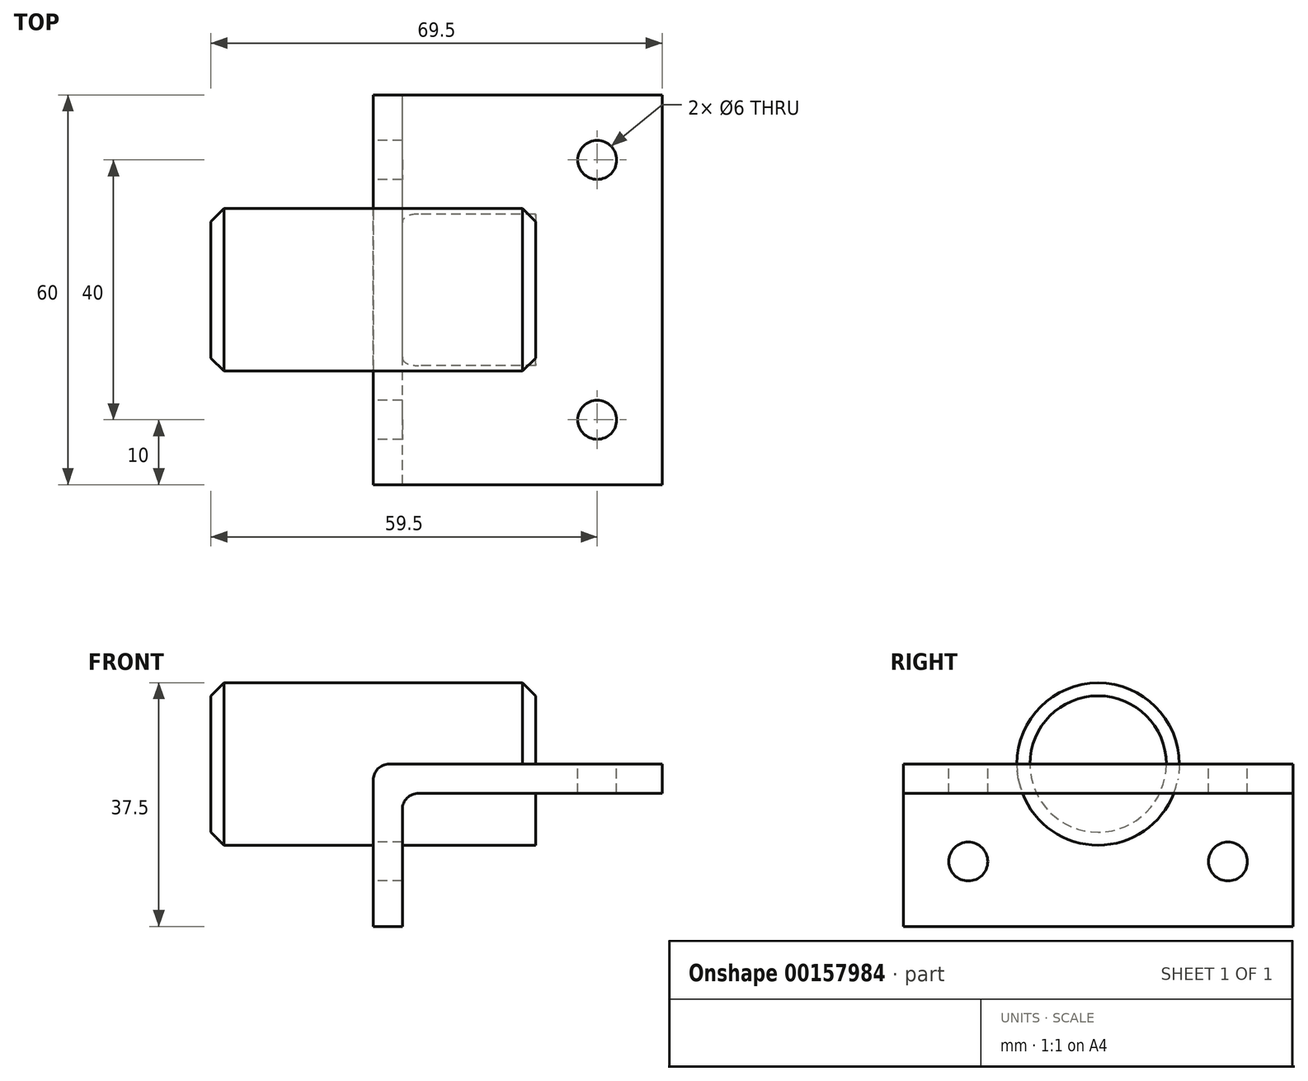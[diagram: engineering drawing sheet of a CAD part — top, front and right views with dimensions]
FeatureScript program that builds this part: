
annotation { "Feature Type Name" : "Feature", "Feature Type Description" : "" }
export const myFeature = defineFeature(function(context is Context, id is Id, definition is map)
    precondition{}
    {
        {
            var Q0;
            Q0=qCreatedBy(makeId("Front.planeOp"),FACE);
            var sketch = newSketch(context, id + "F0", { "sketchPlane" : qUnion([Q0])});
            skLineSegment(sketch, "E0", {"start": v(2.5, 0) * mm, "end": v(44.5, 0) * mm});
            skLineSegment(sketch, "E1", {"start": v(44.5, 0) * mm, "end": v(44.5, -4.5) * mm});
            skLineSegment(sketch, "E2", {"start": v(44.5, -4.5) * mm, "end": v(7, -4.5) * mm});
            skLineSegment(sketch, "E3", {"start": v(4.5, -7) * mm, "end": v(4.5, -25) * mm});
            skLineSegment(sketch, "E4", {"start": v(4.5, -25) * mm, "end": v(0, -25) * mm});
            skLineSegment(sketch, "E5", {"start": v(0, -25) * mm, "end": v(0, -2.5) * mm});
            skPoint(sketch, "E6.visualSharp", {"position": v(4.5, -4.5) * mm});
            skArc(sketch, "E6.filletArc", {"start": v(7, -4.5) * mm, "mid": v(5.23, -5.23) * mm, "end": v(4.5, -7) * mm});
            skPoint(sketch, "E7.visualSharp", {"position": v(0, 0) * mm});
            skArc(sketch, "E7.filletArc", {"start": v(2.5, 0) * mm, "mid": v(0.73, -0.73) * mm, "end": v(0, -2.5) * mm});
            skSolve(sketch);
        }
        {
            var Q0;
            Q0 = qSketchRegion(id + "F0", true);
            extrude(context, id + "F1", {"entities" : qUnion([Q0]), "endBound" : BoundingType.SYMMETRIC, "depth" : 60 * mm});
        }
        {
            var Q0;
            Q0=qCreatedBy(makeId("Right.planeOp"),FACE);
            var sketch = newSketch(context, id + "F2", { "sketchPlane" : qUnion([Q0])});
            skCircle(sketch, "E8", {"center": v(0, 0) * mm, "radius": 12.5 * mm});
            skSolve(sketch);
        }
        {
            var Q0;
            Q0 = qSketchRegion(id + "F2", true);
            extrude(context, id + "F3", {"entities" : qUnion([Q0]), "operationType" : NewBodyOperationType.ADD, "depth" : 25 * mm, "hasSecondDirection" : true, "secondDirectionOppositeDirection" : true, "secondDirectionDepth" : 25 * mm});
        }
        {
            var Q0;
            Q0=makeQuery(id+"F3.opExtrude","CAP_EDGE",EDGE,{"disambiguationData":[OSD([sQuery(id+"F2.wireOp",EDGE,"E8")])],"isStart":true});
            var Q1;
            {var subQ0=sQuery(id+"F2.wireOp",EDGE,"E8");Q1=makeQuery(id+"F3.boolean.opBoolean","SPLIT",EDGE,{"disambiguationData":[TD([makeQuery(id+"F1.opExtrude","SWEPT_FACE",FACE,{"disambiguationData":[OSD([sQuery(id+"F0.wireOp",EDGE,"E0")])]})])],"derivedFrom":makeQuery(id+"F3.opExtrude","CAP_EDGE",EDGE,{"disambiguationData":[OSD([subQ0])],"isStart":false})});}
            chamfer(context, id + "F4", {"entities" : qUnion([Q0, Q1]), "width" : 2 * mm, "tangentPropagation" : true});
        }
        {
            var Q0;
            Q0=makeQuery(id+"F1.opExtrude","SWEPT_FACE",FACE,{"disambiguationData":[OSD([sQuery(id+"F0.wireOp",EDGE,"E5")])]});
            var sketch = newSketch(context, id + "F5", { "sketchPlane" : qUnion([Q0])});
            skCircle(sketch, "E9", {"center": v(-20, -15) * mm, "radius": 3 * mm});
            skCircle(sketch, "E10", {"center": v(20, -15) * mm, "radius": 3 * mm});
            skSolve(sketch);
        }
        {
            var Q0;
            Q0 = qSketchRegion(id + "F5", true);
            extrude(context, id + "F6", {"entities" : qUnion([Q0]), "operationType" : NewBodyOperationType.REMOVE, "endBound" : BoundingType.THROUGH_ALL, "oppositeDirection" : true, "depth" : 25 * mm});
        }
        {
            var Q0;
            Q0=makeQuery(id+"F1.opExtrude","SWEPT_FACE",FACE,{"disambiguationData":[OSD([sQuery(id+"F0.wireOp",EDGE,"E0")])]});
            var sketch = newSketch(context, id + "F7", { "sketchPlane" : qUnion([Q0])});
            skCircle(sketch, "E11", {"center": v(34.5, 20) * mm, "radius": 3 * mm});
            skCircle(sketch, "E12", {"center": v(34.5, -20) * mm, "radius": 3 * mm});
            skSolve(sketch);
        }
        {
            var Q0;
            Q0 = qSketchRegion(id + "F7", true);
            extrude(context, id + "F8", {"entities" : qUnion([Q0]), "operationType" : NewBodyOperationType.REMOVE, "endBound" : BoundingType.THROUGH_ALL, "oppositeDirection" : true, "depth" : 25 * mm});
        }
    });
